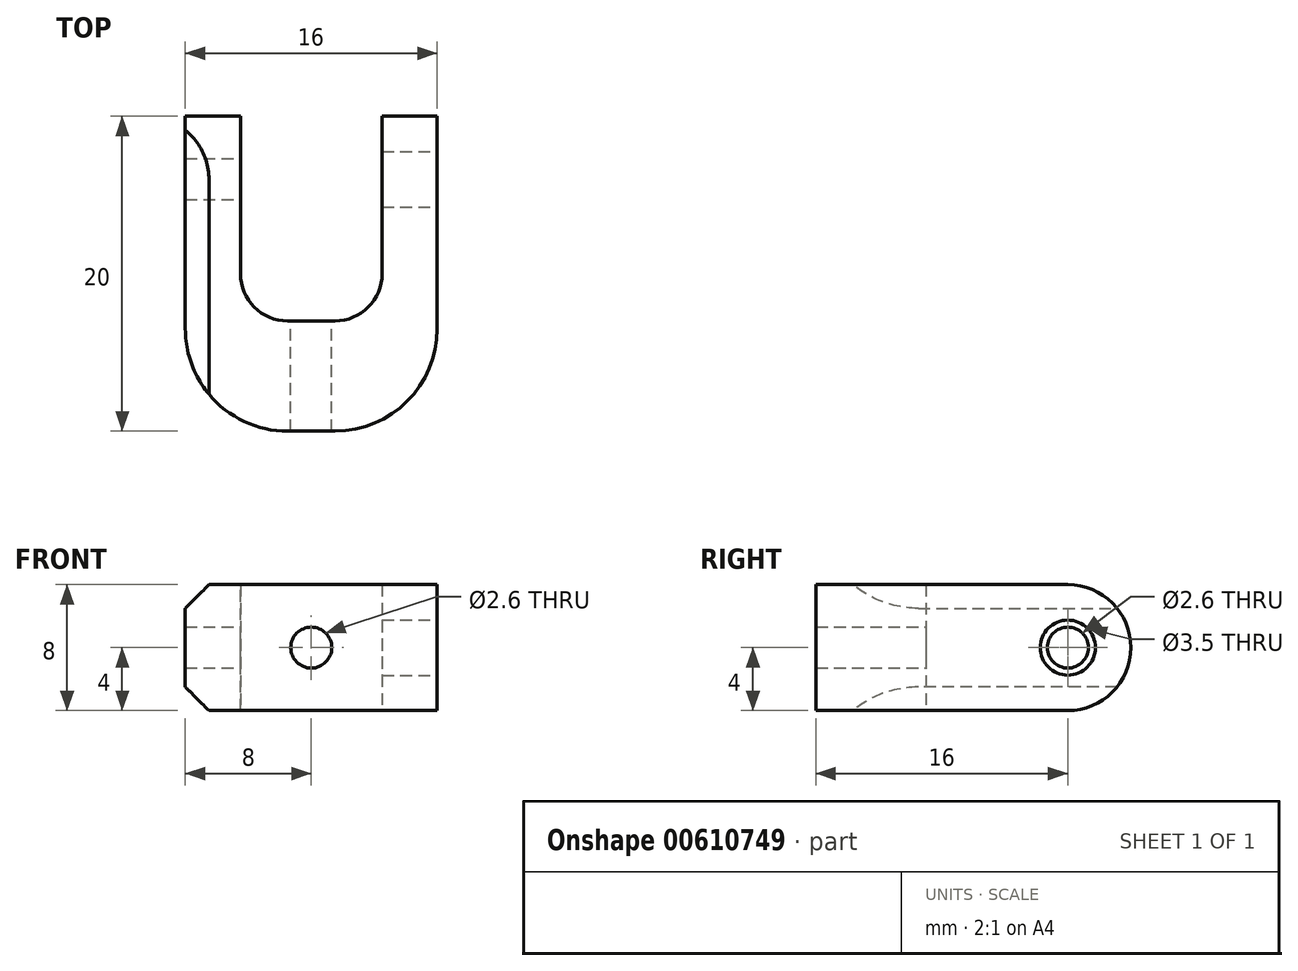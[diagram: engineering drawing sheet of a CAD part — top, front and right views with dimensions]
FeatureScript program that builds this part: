
annotation { "Feature Type Name" : "Feature", "Feature Type Description" : "" }
export const myFeature = defineFeature(function(context is Context, id is Id, definition is map)
    precondition{}
    {
        {
            var Q0;
            Q0=qCreatedBy(makeId("Top.planeOp"),FACE);
            var sketch = newSketch(context, id + "F0", { "sketchPlane" : qUnion([Q0])});
            skLineSegment(sketch, "E0", {"start": v(-4.5, 13) * mm, "end": v(-4.5, 3) * mm});
            skLineSegment(sketch, "E1", {"start": v(-1.5, 0) * mm, "end": v(1.5, 0) * mm});
            skLineSegment(sketch, "E2", {"start": v(4.5, 3) * mm, "end": v(4.5, 13) * mm});
            skLineSegment(sketch, "E3", {"start": v(4.5, 13) * mm, "end": v(8, 13) * mm});
            skLineSegment(sketch, "E4", {"start": v(8, 13) * mm, "end": v(8, -0.5) * mm});
            skLineSegment(sketch, "E5", {"start": v(0, 0) * mm, "end": v(0, 9.52) * mm, "construction": true});
            skLineSegment(sketch, "E6.MirrorCS", {"start": v(-4.5, 13) * mm, "end": v(-8, 13) * mm});
            skLineSegment(sketch, "E7.MirrorCS", {"start": v(-8, 13) * mm, "end": v(-8, -0.5) * mm});
            skLineSegment(sketch, "E8", {"start": v(-1.5, -7) * mm, "end": v(1.5, -7) * mm});
            skPoint(sketch, "E9.visualSharp", {"position": v(4.5, 0) * mm});
            skArc(sketch, "E9.filletArc", {"start": v(1.5, 0) * mm, "mid": v(3.62, 0.88) * mm, "end": v(4.5, 3) * mm});
            skPoint(sketch, "E10.visualSharp", {"position": v(-4.5, 0) * mm});
            skArc(sketch, "E10.filletArc", {"start": v(-4.5, 3) * mm, "mid": v(-3.62, 0.88) * mm, "end": v(-1.5, 0) * mm});
            skPoint(sketch, "E11.visualSharp", {"position": v(-8, -7) * mm});
            skArc(sketch, "E11.filletArc", {"start": v(-8, -0.5) * mm, "mid": v(-6.1, -5.1) * mm, "end": v(-1.5, -7) * mm});
            skPoint(sketch, "E12.visualSharp", {"position": v(8, -7) * mm});
            skArc(sketch, "E12.filletArc", {"start": v(1.5, -7) * mm, "mid": v(6.1, -5.1) * mm, "end": v(8, -0.5) * mm});
            skSolve(sketch);
        }
        {
            var Q0;
            Q0 = qSketchRegion(id + "F0", true);
            extrude(context, id + "F1", {"entities" : qUnion([Q0]), "depth" : 8 * mm, "offsetDistance" : 25 * mm});
        }
        {
            var Q0;
            Q0=makeQuery(id+"F1.opExtrude","SWEPT_FACE",FACE,{"disambiguationData":[OSD([sQuery(id+"F0.wireOp",EDGE,"E4")])]});
            var sketch = newSketch(context, id + "F2", { "sketchPlane" : qUnion([Q0])});
            skArc(sketch, "E13", {"start": v(9, 0) * mm, "mid": v(13, 4) * mm, "end": v(9, 8) * mm});
            skCircle(sketch, "E14", {"center": v(9, 4) * mm, "radius": 1.3 * mm});
            skCircle(sketch, "E15", {"center": v(9, 4) * mm, "radius": 1.75 * mm});
            skSolve(sketch);
        }
        {
            var Q0;
            {var subQ0=sQuery(id+"F2.wireOp",EDGE,"E13");var subQ1=sQuery(id+"F0.wireOp",EDGE,"E4");var subQ2=makeQuery(id+"F1.opExtrude","CAP_EDGE",EDGE,{"disambiguationData":[OSD([subQ1])],"isStart":true});var subQ3=makeQuery(id+"F2.imprint","INTERSECT",VERTEX,{"derivedFrom":[subQ2,subQ0]});Q0=makeQuery(id+"F2.imprint","IMPRINT",FACE,{"disambiguationData":[TD([[makeQuery(id+"F2.imprint","IMPRINT",EDGE,{"disambiguationData":[TD([[subQ3,-1.0]])],"derivedFrom":subQ0}),-1.0]])]});}
            var Q1;
            {var subQ0=sQuery(id+"F2.wireOp",EDGE,"E13");var subQ1=sQuery(id+"F0.wireOp",EDGE,"E4");var subQ2=makeQuery(id+"F1.opExtrude","CAP_EDGE",EDGE,{"disambiguationData":[OSD([subQ1])],"isStart":false});var subQ3=makeQuery(id+"F2.imprint","INTERSECT",VERTEX,{"derivedFrom":[subQ2,subQ0]});Q1=makeQuery(id+"F2.imprint","IMPRINT",FACE,{"disambiguationData":[TD([[makeQuery(id+"F2.imprint","IMPRINT",EDGE,{"disambiguationData":[TD([[subQ3,1.0]])],"derivedFrom":subQ0}),-1.0]])]});}
            extrude(context, id + "F3", {"entities" : qUnion([Q0, Q1]), "operationType" : NewBodyOperationType.REMOVE, "endBound" : BoundingType.THROUGH_ALL, "oppositeDirection" : true, "depth" : 25 * mm, "offsetDistance" : 25 * mm});
        }
        {
            var Q0;
            Q0=makeQuery(id+"F2.imprint","IMPRINT",FACE,{"disambiguationData":[TD([[makeQuery(id+"F2.imprint","IMPRINT",EDGE,{"derivedFrom":sQuery(id+"F2.wireOp",EDGE,"E14")}),1.0]])]});
            extrude(context, id + "F4", {"entities" : qUnion([Q0]), "operationType" : NewBodyOperationType.REMOVE, "endBound" : BoundingType.THROUGH_ALL, "oppositeDirection" : true, "depth" : 25 * mm, "offsetDistance" : 25 * mm});
        }
        {
            var Q0;
            Q0=makeQuery(id+"F2.imprint","IMPRINT",FACE,{"disambiguationData":[TD([[makeQuery(id+"F2.imprint","IMPRINT",EDGE,{"derivedFrom":sQuery(id+"F2.wireOp",EDGE,"E14")}),-1.0]])]});
            extrude(context, id + "F5", {"entities" : qUnion([Q0]), "operationType" : NewBodyOperationType.REMOVE, "endBound" : BoundingType.UP_TO_NEXT, "oppositeDirection" : true, "depth" : 25 * mm, "offsetDistance" : 25 * mm});
        }
        {
            var Q0;
            Q0=makeQuery(id+"F1.opExtrude","SWEPT_FACE",FACE,{"disambiguationData":[OSD([sQuery(id+"F0.wireOp",EDGE,"E1")])]});
            var sketch = newSketch(context, id + "F6", { "sketchPlane" : qUnion([Q0])});
            skLineSegment(sketch, "E16", {"start": v(-1.5, 8) * mm, "end": v(1.5, 0) * mm, "construction": true});
            skCircle(sketch, "E17", {"center": v(0, 4) * mm, "radius": 1.3 * mm});
            skSolve(sketch);
        }
        {
            var Q0;
            Q0 = qSketchRegion(id + "F6", true);
            extrude(context, id + "F7", {"entities" : qUnion([Q0]), "operationType" : NewBodyOperationType.REMOVE, "endBound" : BoundingType.UP_TO_NEXT, "oppositeDirection" : true, "depth" : 25 * mm, "offsetDistance" : 25 * mm});
        }
        {
            var Q0;
            Q0=makeQuery(id+"F1.opExtrude","CAP_EDGE",EDGE,{"disambiguationData":[OSD([sQuery(id+"F0.wireOp",EDGE,"E7.MirrorCS")])],"isStart":true});
            var Q1;
            Q1=makeQuery(id+"F1.opExtrude","CAP_EDGE",EDGE,{"disambiguationData":[OSD([sQuery(id+"F0.wireOp",EDGE,"E7.MirrorCS")])],"isStart":false});
            chamfer(context, id + "F8", {"entities" : qUnion([Q0, Q1]), "width" : 1.5 * mm});
        }
    });
